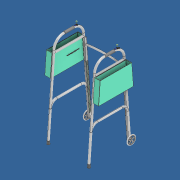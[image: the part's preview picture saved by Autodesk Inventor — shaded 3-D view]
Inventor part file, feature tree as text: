
AUTODESK INVENTOR PART (.ipt)
format: ipt  version: 2021 (Build 250183000, 183)  size: 1,208,320 bytes
history: native  units: in
note: dims shown in document units (in); Inventor stores cm internally (conversion verified against a paired STEP export)
features: extrude x11, sketch x11, plane x5, fillet x3, mirror x3, revolve x1, sweep x1
ambient origin geometry x8: Origin, YZ Plane, XZ Plane, XY Plane, X Axis, Y Axis, Z Axis, Center Point
bodies: Solid1 (feature_tree)
feature tree (35):
  plane  "Work Plane1"
  extrude  "Extrusion1"  Depth=0.2756in TaperAngle=0.0deg
  extrude  "Extrusion2"  Depth=0.3937in
  extrude  "Extrusion3"  Depth=10.2445in
  plane  "Work Plane2"
  fillet  "Fillet1"  [1 undecoded]
  mirror  "Mirror1"
  plane  "Work Plane3"
  extrude  "Extrusion4"  Depth=2.3622in TaperAngle=0.0deg
  fillet  "Fillet2"  Radius=0.1969in
  extrude  "Extrusion5"  Depth=31.0625in
  extrude  "Extrusion6"  Depth=0.3543in
  mirror  "Mirror2"
  plane  "Work Plane4"
  extrude  "Extrusion7"  Depth=0.3937in
  fillet  "Fillet3"  Radius=0.1969in
  extrude  "Extrusion8"  Depth=0.2165in
  extrude  "Extrusion9"  Depth=0.4724in
  extrude  "Extrusion10"  Depth=0.2559in
  plane  "Work Plane5"
  revolve  "Revolution1"  [1 undecoded]
  mirror  "Mirror3"
  extrude  "Extrusion11"  Depth=0.3937in
  sketch  "Sketch1"  dims[d0=0.4375in d1=0.2756in d2=0.0in]
  sketch  "Sketch2"  dims[d6=0.3937in d7=0.3937in]
  sketch  "Sketch3"  dims[d8=10.2445in d9=10.2445in d10=180.0deg]
  sketch  "Sketch5"  dims[d11=180.0deg d12=2.3622in d13=0.0in d14=0.1969in d15=0.0in]
  sketch  "Sketch6"  dims[d16=-10.0in d17=0.0787in d18=31.0625in]
  sketch  "Sketch7"  dims[d21=0.1582in d22=0.3543in]
  sketch  "Sketch8"  dims[d23=0.1773in d24=0.3937in d25=0.1969in]
  sketch  "Sketch9"  dims[d26=0.4331in d27=0.2165in]
  sketch  "Sketch10"  dims[d28=0.4724in d29=0.2362in]
  sketch  "Sketch11"  dims[d30=0.5118in d31=0.2559in]
  sketch  "Sketch12"  dims[d32=0.5512in d33=0.5906in d34=0.2362in d35=0.2362in d36=0.2362in d37=0.2362in d38=0.2362in d39=0.2362in d40=0.2362in d41=0.2362in d43=0.5315in d44=0.5709in d45=0.6102in d46=0.6496in d47=0.689in d48=0.7283in d50=0.1378in d51=0.3543in d52=0.3937in d53=0.4331in d54=0.4724in d55=0.5118in d56=0.5512in d57=0.5906in d58=0.6299in d59=0.6693in d60=0.0394in d61=0.1181in d63=0.0394in d66=0.0394in d67=0.0394in d68=0.0394in d69=0.0394in d70=0.0394in d71=0.1181in d72=0.315in d73=0.0in d74=0.0787in d75=6.0236in d76=0.2953in d77=0.2756in d79=0.0394in d86=0.5485in d87=0.5085in d88=0.5847in d89=7.4606in d90=35.5906in d91=90.0deg d92=0.7087in d93=10.2362in d95=0.1378in d96=0.8268in d97=0.0in d98=0.5118in d99=0.0in d100=41.6875in d102=0.5906in d103=0.5512in d104=0.0in d105=0.0787in d106=0.5512in d107=0.3937in d109=0.0in d110=0.2756in d111=1.5748in d112=0.8268in d113=0.0in d114=0.0394in d115=0.0394in d116=0.0394in d117=0.0394in d118=0.0787in d119=0.0in d120=0.4724in d121=0.6496in d122=0.1575in d123=0.0in d124=-0.2756in d129=0.3937in d130=1.5733in d131=0.7904in d132=90.0deg d133=1.7821in d134=1.9685in d135=0.0in]
  sweep  "Sweep5"
note: 2 required parameter values undecoded (feature->parameter linkage not recoverable at this tier; creation-order binding heuristic only, values carry confidence <= 0.55)